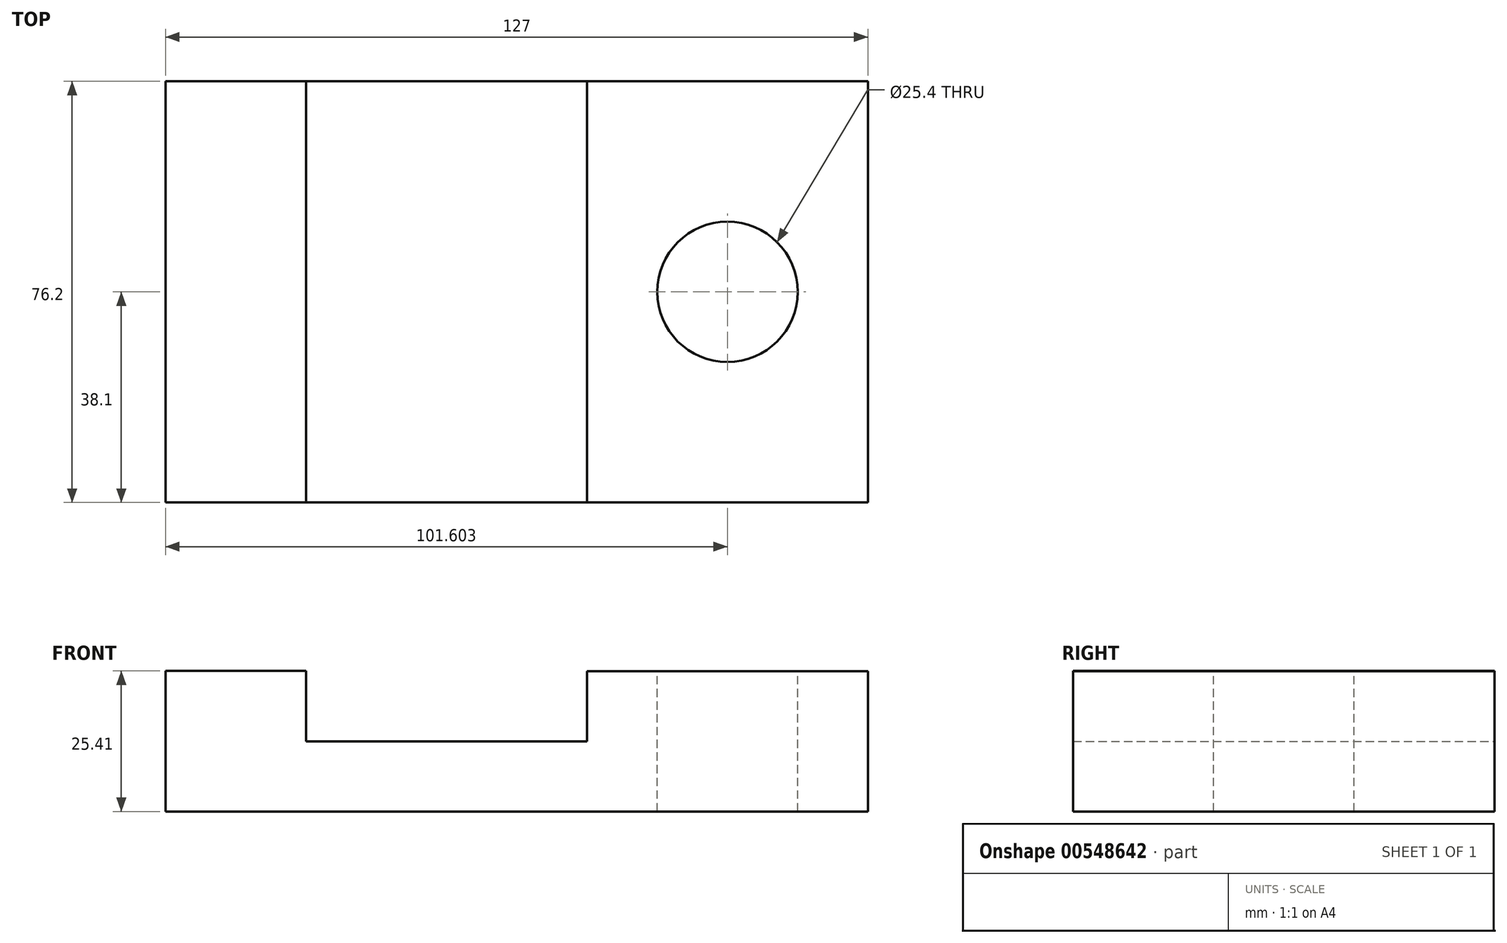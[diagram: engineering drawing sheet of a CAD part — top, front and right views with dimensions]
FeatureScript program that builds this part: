
annotation { "Feature Type Name" : "Feature", "Feature Type Description" : "" }
export const myFeature = defineFeature(function(context is Context, id is Id, definition is map)
    precondition{}
    {
        {
            var Q0;
            Q0=qCreatedBy(makeId("Front.planeOp"),FACE);
            var sketch = newSketch(context, id + "F0", { "sketchPlane" : qUnion([Q0])});
            skLineSegment(sketch, "E0", {"start": v(-75.32, 17.97) * mm, "end": v(-49.9, 17.97) * mm});
            skLineSegment(sketch, "E1", {"start": v(-75.32, 17.97) * mm, "end": v(-75.32, -7.44) * mm});
            skLineSegment(sketch, "E2", {"start": v(-49.9, 17.97) * mm, "end": v(-49.9, 5.26) * mm});
            skLineSegment(sketch, "E3", {"start": v(-75.32, -7.44) * mm, "end": v(51.68, -7.44) * mm});
            skLineSegment(sketch, "E4", {"start": v(51.68, -7.44) * mm, "end": v(51.68, 17.96) * mm});
            skLineSegment(sketch, "E5", {"start": v(51.68, 17.96) * mm, "end": v(0.88, 17.96) * mm});
            skLineSegment(sketch, "E6", {"start": v(0.88, 5.26) * mm, "end": v(0.88, 17.96) * mm});
            skLineSegment(sketch, "E7", {"start": v(-49.9, 5.26) * mm, "end": v(0.88, 5.26) * mm});
            skSolve(sketch);
        }
        {
            var Q0;
            Q0 = qSketchRegion(id + "F0", true);
            extrude(context, id + "F1", {"entities" : qUnion([Q0]), "depth" : 76.2 * mm, "offsetDistance" : 25.4 * mm});
        }
        {
            var Q0;
            Q0=makeQuery(id+"F1.opExtrude","SWEPT_FACE",FACE,{"disambiguationData":[OSD([sQuery(id+"F0.wireOp",EDGE,"E5")])]});
            var sketch = newSketch(context, id + "F2", { "sketchPlane" : qUnion([Q0])});
            skCircle(sketch, "E8", {"center": v(26.28, -38.1) * mm, "radius": 12.7 * mm});
            skPoint(sketch, "E8.centerSnap0", {"position": v(0.88, -38.1) * mm});
            skPoint(sketch, "E8.centerSnap1", {"position": v(26.28, -76.2) * mm});
            skSolve(sketch);
        }
        {
            var Q0;
            Q0 = qSketchRegion(id + "F2", true);
            extrude(context, id + "F3", {"entities" : qUnion([Q0]), "operationType" : NewBodyOperationType.REMOVE, "endBound" : BoundingType.THROUGH_ALL, "oppositeDirection" : true, "depth" : 25.4 * mm, "offsetDistance" : 25.4 * mm});
        }
    });
